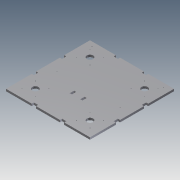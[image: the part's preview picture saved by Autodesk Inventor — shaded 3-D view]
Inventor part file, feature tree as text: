
AUTODESK INVENTOR PART (.ipt)
format: ipt  version: 2011 (Build 150239000, 239)  size: 1,268,736 bytes
history: native  units: in
note: dims shown in document units (in); Inventor stores cm internally (conversion verified against a paired STEP export)
features: sketch x40, extrude x39
ambient origin geometry x8: Origin, YZ Plane, XZ Plane, XY Plane, X Axis, Y Axis, Z Axis, Center Point
bodies: Solid1 (feature_tree)
feature tree (79):
  sketch  "Sketch1"  dims[d0=20.0in d1=20.0in]
  extrude  "Extrusion1"  Depth=20.0in
  extrude  "Extrusion2"  Depth=3.5in
  extrude  "Extrusion3"  Depth=3.5in
  extrude  "Extrusion4"  Depth=3.5in
  extrude  "Extrusion5"  Depth=3.5in
  extrude  "Extrusion6"  Depth=1.911in
  extrude  "Extrusion7"  Depth=5.089in
  extrude  "Extrusion8"  Depth=5.089in
  extrude  "Extrusion9"  Depth=1.911in
  extrude  "Extrusion10"  Depth=0.156in
  extrude  "Extrusion11"  Depth=0.156in
  extrude  "Extrusion12"  Depth=0.156in
  extrude  "Extrusion13"  Depth=0.156in
  extrude  "Extrusion14"  Depth=0.156in
  extrude  "Extrusion15"  Depth=0.156in
  extrude  "Extrusion16"  Depth=0.156in
  extrude  "Extrusion17"  Depth=0.156in
  extrude  "Extrusion18"  Depth=1.0in
  extrude  "Extrusion19"  Depth=1.0in
  extrude  "Extrusion20"  Depth=0.5in TaperAngle=0.0deg
  extrude  "Extrusion21"  Depth=0.5in
  extrude  "Extrusion22"  Depth=1.5in
  extrude  "Extrusion23"  Depth=1.5in
  extrude  "Extrusion24"  Depth=1.5in
  extrude  "Extrusion25"  Depth=1.5in
  extrude  "Extrusion26"  Depth=1.5in
  extrude  "Extrusion27"  Depth=1.5in
  extrude  "Extrusion28"  Depth=1.5in
  extrude  "Extrusion29"  Depth=1.0in TaperAngle=0.0deg
  extrude  "Extrusion30"  Depth=0.5in TaperAngle=0.0deg
  extrude  "Extrusion31"  Depth=0.25in TaperAngle=0.0deg
  extrude  "Extrusion32"  Depth=2.6in
  extrude  "Extrusion33"  Depth=7.4in
  extrude  "Extrusion34"  Depth=0.25in
  extrude  "Extrusion35"  Depth=0.25in
  extrude  "Extrusion36"  Depth=0.25in
  extrude  "Extrusion37"  Depth=0.25in
  extrude  "Extrusion38"  Depth=0.25in
  extrude  "Extrusion39"  Depth=0.25in
  sketch  "Sketch2"  dims[d2=3.5in d3=3.5in]
  sketch  "Sketch3"  dims[d4=3.5in d5=3.5in]
  sketch  "Sketch4"  dims[d6=3.5in d7=3.5in]
  sketch  "Sketch5"  dims[d8=3.5in d9=3.5in]
  sketch  "Sketch6"  dims[d10=1.911in d11=1.911in]
  sketch  "Sketch7"  dims[d12=1.911in d13=5.089in]
  sketch  "Sketch8"  dims[d14=5.089in d15=5.089in]
  sketch  "Sketch9"  dims[d16=5.089in d17=1.911in]
  sketch  "Sketch10"  dims[d18=1.911in d19=0.156in]
  sketch  "Sketch11"  dims[d20=0.156in d21=0.156in]
  sketch  "Sketch12"  dims[d22=0.156in d23=0.156in]
  sketch  "Sketch13"  dims[d24=0.156in d25=0.156in]
  sketch  "Sketch14"  dims[d26=0.156in d27=0.156in]
  sketch  "Sketch15"  dims[d28=0.156in d29=0.156in]
  sketch  "Sketch16"  dims[d30=0.156in d31=0.156in]
  sketch  "Sketch17"  dims[d32=0.156in d33=0.156in]
  sketch  "Sketch18"  dims[d34=0.156in d35=1.0in]
  sketch  "Sketch19"  dims[d36=1.0in d37=1.0in]
  sketch  "Sketch20"  dims[d38=1.0in d39=0.5in d40=0.0in]
  sketch  "Sketch21"  dims[d41=0.5in d42=0.5in]
  sketch  "Sketch22"  dims[d43=1.0in d44=1.5in]
  sketch  "Sketch23"  dims[d45=1.0in d46=1.5in]
  sketch  "Sketch24"  dims[d47=1.0in d48=1.5in]
  sketch  "Sketch25"  dims[d49=1.0in d50=1.5in]
  sketch  "Sketch26"  dims[d51=1.0in d52=1.5in]
  sketch  "Sketch27"  dims[d53=1.0in d54=1.5in]
  sketch  "Sketch28"  dims[d55=1.0in d56=1.5in]
  sketch  "Sketch29"  dims[d57=1.0in d58=1.0in d59=0.0in]
  sketch  "Sketch30"  dims[d60=1.0in d61=0.0in d62=0.5in d63=0.0in]
  sketch  "Sketch31"  dims[d64=0.5in d65=0.0in d66=0.25in d67=0.0in]
  sketch  "Sketch32"  dims[d68=10.0in d69=2.6in]
  sketch  "Sketch33"  dims[d70=5.2in d71=7.4in]
  sketch  "Sketch34"  dims[d72=5.2in d73=0.25in]
  sketch  "Sketch35"  dims[d74=0.25in d75=0.25in]
  sketch  "Sketch36"  dims[d76=0.25in d77=0.25in]
  sketch  "Sketch37"  dims[d78=0.25in d79=0.25in]
  sketch  "Sketch38"  dims[d80=0.25in d81=0.25in]
  sketch  "Sketch39"  dims[d82=0.25in d83=0.25in]
  sketch  "Sketch40"  dims[d84=0.25in d85=0.25in d86=0.0in d87=1.5in d88=1.5in d89=1.5in d90=1.5in d91=0.25in d92=0.25in d93=0.25in d94=0.25in d95=0.25in d96=0.25in d97=0.25in d98=0.25in d99=0.25in d100=0.25in d101=0.25in d102=0.25in d103=0.0in d104=1.0in d105=1.0in d106=1.0in d107=1.0in d108=1.0in d109=1.0in d110=1.0in d111=1.0in d112=1.0in d113=1.0in d114=1.0in d115=1.0in d116=1.0in d117=1.0in d118=1.0in d119=1.0in d120=1.0in d121=1.0in d122=1.0in d123=1.0in d124=0.25in d125=1.0in d126=0.0in d127=1.0in d128=0.0in d129=1.5in d130=1.0in d131=0.0in d132=0.25in d133=0.25in d134=0.25in d135=0.25in d136=0.25in d137=0.25in d138=0.25in d139=0.25in d140=0.25in d141=0.25in d142=0.25in d143=0.25in d144=0.25in d145=0.0in d146=0.25in d147=0.0in d148=0.25in d149=1.5in d150=1.25in d151=1.0in d152=2.0in d153=1.0in d154=2.0in d155=1.0in d156=2.0in d157=1.0in d158=0.345in d159=0.25in d160=0.0in d161=0.25in d162=0.0in d163=2.25in d164=0.25in d165=1.0in d166=3.0in d167=1.0in d168=3.0in d169=1.0in d170=3.0in d171=1.0in d172=3.0in d173=1.0in d174=0.25in d175=0.0in d176=0.25in d177=0.25in d178=0.25in d179=0.0in d180=0.25in d181=0.25in d182=0.5in d183=0.5in d184=0.25in d185=0.0in d186=0.25in d187=0.0in d188=0.25in d189=0.0in d190=0.25in d191=0.0in d192=1.0in d193=1.0in d194=0.25in d195=3.25in d196=1.0in d197=3.0in d198=1.0in d199=3.0in d200=1.0in d201=3.25in d202=1.0in d203=0.5in d204=0.5in d205=0.5in d206=0.5in d207=0.25in d208=0.0in d209=0.25in d210=0.0in d211=1.594in d212=1.594in d213=3.188in d214=3.188in d215=1.594in d216=1.594in d217=3.188in d218=3.188in d219=0.156in d220=0.156in d221=0.156in d222=0.156in d223=0.156in d224=0.156in d225=0.156in d226=0.156in d227=0.156in d228=0.156in d229=0.156in d230=0.156in d231=0.156in d232=0.156in d233=0.156in d234=0.156in d235=0.25in d236=0.0in d237=0.25in d238=0.0in d239=0.25in d240=0.0in d241=0.25in d242=0.0in d243=6.65in d244=6.7in d245=0.5in d246=0.5in d247=0.0in d248=0.5in d249=0.5in d250=0.5in d251=0.5in d252=0.0in d253=0.25in d254=0.25in d255=0.5in d256=0.0in d257=0.25in d258=0.5in d259=0.0in d260=0.25in d261=0.5in d262=0.0in d263=0.25in d264=0.25in d265=0.5in d266=0.0in d267=3.85in d268=7.7in d269=0.5in d270=1.0in d271=1.0in d272=0.5in d273=0.5in d274=1.0in d275=0.0in d276=9.0in d277=7.7in d278=0.5in d279=1.0in d280=9.0in d281=0.5in d282=1.0in d283=0.0in d284=1.5in d285=1.0in d286=0.156in d287=1.5in d288=1.0in d289=0.156in d290=1.0in d291=0.0in d292=10.35in d293=1.0in d294=1.0in d295=1.0in d296=1.0in d297=0.156in d298=0.156in d299=1.0in d300=0.0in d301=0.315in d302=0.3937in d303=1.1811in d304=1.0in d305=0.0in d306=4.3307in d307=0.8465in d308=1.6929in d309=0.1969in d310=1.25in d311=0.0984in d312=0.156in d313=0.156in d314=1.0in d315=0.0in]
